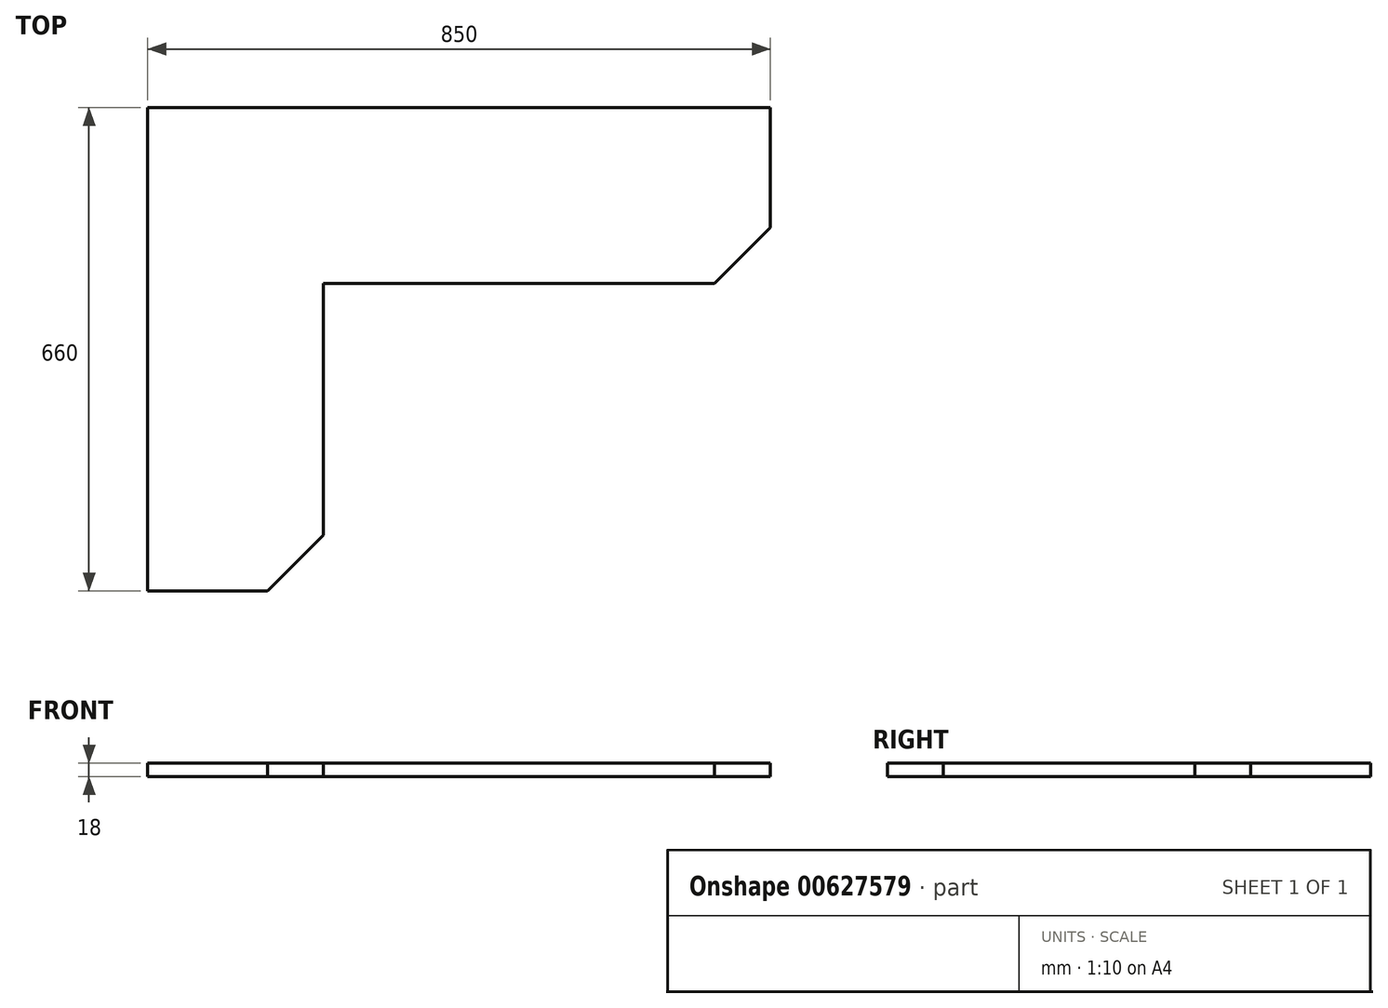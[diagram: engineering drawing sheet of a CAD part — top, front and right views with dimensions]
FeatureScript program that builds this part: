
annotation { "Feature Type Name" : "Feature", "Feature Type Description" : "" }
export const myFeature = defineFeature(function(context is Context, id is Id, definition is map)
    precondition{}
    {
        {
            var Q0;
            Q0=qCreatedBy(makeId("Top.planeOp"),FACE);
            var sketch = newSketch(context, id + "F0", { "sketchPlane" : qUnion([Q0])});
            skLineSegment(sketch, "E0", {"start": v(0, 0) * mm, "end": v(0, 660) * mm});
            skLineSegment(sketch, "E1", {"start": v(0, 660) * mm, "end": v(850, 660) * mm});
            skLineSegment(sketch, "E2", {"start": v(850, 660) * mm, "end": v(850, 496.2) * mm});
            skLineSegment(sketch, "E3", {"start": v(773.8, 420) * mm, "end": v(240, 420) * mm});
            skLineSegment(sketch, "E4", {"start": v(240, 420) * mm, "end": v(240, 76.2) * mm});
            skLineSegment(sketch, "E5", {"start": v(163.8, 0) * mm, "end": v(0, 0) * mm});
            skLineSegment(sketch, "E6", {"start": v(163.8, 0) * mm, "end": v(240, 76.2) * mm});
            skLineSegment(sketch, "E7", {"start": v(773.8, 420) * mm, "end": v(850, 496.2) * mm});
            skSolve(sketch);
        }
        {
            var Q0;
            Q0 = qSketchRegion(id + "F0", true);
            extrude(context, id + "F1", {"entities" : qUnion([Q0]), "depth" : 18 * mm, "offsetDistance" : 25.4 * mm});
        }
    });
